# Revit family: VTi.908.I_Пресс-фитинг_Накид Гайка_Нерж_VALTEC
name_source: partatom
category: Соединительные детали трубопроводов
units: mm (PartAtom-declared; Revit-internal decimal feet)

## family parameters
Всегда вертикально = Да
На основе рабочей плоскости = Нет
Общий = Нет
При загрузке вырезать с полостями = Нет
Размер круглого соединителя = Использовать диаметр
Тип детали = Соединение

## types (13) — shared parameters
ADSK_Единица измерения = шт.
ADSK_Количество = 1
ADSK_Материал = Сталь, нержавеющая - VALTEC
LT = VTi.908.I_Пресс-фитинг_Накид Гайка_Нерж_VALTEC
zero-valued in all types: Отметка по умолчанию

## type names (no varying parameters)
- Пресс-фитинг из нержавеющей стали с накидной гайкой 12 мм х 1/2"
- Пресс-фитинг из нержавеющей стали с накидной гайкой 15 мм х 1/2"
- Пресс-фитинг из нержавеющей стали с накидной гайкой 15 мм х 3/4"
- Пресс-фитинг из нержавеющей стали с накидной гайкой 18 мм х 1/2"
- Пресс-фитинг из нержавеющей стали с накидной гайкой 18 мм х 3/4"
- Пресс-фитинг из нержавеющей стали с накидной гайкой 22 мм х 1/2"
- Пресс-фитинг из нержавеющей стали с накидной гайкой 22 мм х 3/4"
- Пресс-фитинг из нержавеющей стали с накидной гайкой 28 мм х 1"
- Пресс-фитинг из нержавеющей стали с накидной гайкой 28 мм х 3/4"
- Пресс-фитинг из нержавеющей стали с накидной гайкой 35 мм х 1"
- Пресс-фитинг из нержавеющей стали с накидной гайкой 35 мм х 1 1/4"
- Пресс-фитинг из нержавеющей стали с накидной гайкой 42 мм х 1 1/2"
- Пресс-фитинг из нержавеющей стали с накидной гайкой 54мм х 2"
